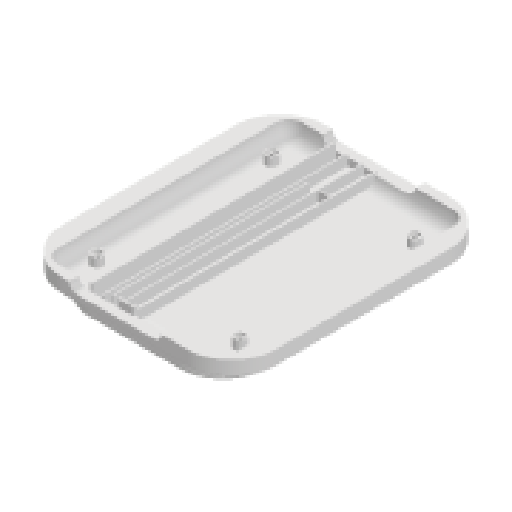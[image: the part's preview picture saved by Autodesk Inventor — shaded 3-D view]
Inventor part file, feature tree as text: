
AUTODESK INVENTOR PART (.ipt)
format: ipt  version: 2024 (Build 280153000, 153)  size: 738,304 bytes
history: native  units: mm
features: fillet x20, extrude x17, sketch x8, hole x1
ambient origin geometry x8: Origin, YZ Plane, XZ Plane, XY Plane, X Axis, Y Axis, Z Axis, Center Point
bodies: Solid1 (feature_tree)
feature tree (46):
  sketch  "Sketch1"  dims[d4=117.2mm d6=1.0mm]
  extrude  "Extrusion1"  Depth=117.2mm
  extrude  "Extrusion4"  Depth=1.0mm
  extrude  "Extrusion5"  Depth=1.0mm
  extrude  "Extrusion8"  Depth=96.0mm
  extrude  "Extrusion9"  Depth=6.8mm
  extrude  "Extrusion14"  Depth=29.9mm
  extrude  "Extrusion15"  Depth=1.0mm
  extrude  "Extrusion16"  Depth=2.0mm
  fillet  "Face Fillet21"
  fillet  "Face Fillet25"
  fillet  "Face Fillet27"
  fillet  "Face Fillet28"
  fillet  "Face Fillet29"
  fillet  "Fillet1"  Radius=177.0mm
  extrude  "Extrusion17"  Depth=2.0mm
  fillet  "Face Fillet30"
  extrude  "Extrusion19"  Depth=2.0mm
  fillet  "Fillet2"  Radius=47.0mm
  extrude  "Extrusion22"  Depth=2.0mm
  extrude  "Extrusion23"  Depth=96.0mm
  fillet  "Fillet6"  Radius=164.2mm
  fillet  "Fillet7"  Radius=12.0mm
  extrude  "Extrusion34"  Depth=2.0mm
  sketch  "Sketch10"  dims[d11=18.7mm d12=96.0mm]
  sketch  "Sketch11"  dims[d13=7.9mm d16=6.8mm]
  extrude  "Extrusion35"  Depth=2.0mm
  extrude  "Extrusion36"  Depth=10.0mm TaperAngle=0.0deg
  extrude  "Extrusion37"  Depth=2.0mm TaperAngle=0.0deg
  fillet  "Fillet8"  Radius=12.0mm
  extrude  "Extrusion38"  Depth=2.0mm TaperAngle=0.0deg
  fillet  "Face Fillet31"
  fillet  "Face Fillet32"
  fillet  "Face Fillet33"
  fillet  "Face Fillet34"
  fillet  "Fillet9"  Radius=4.0mm
  fillet  "Face Fillet35"
  fillet  "Face Fillet36"
  fillet  "Face Fillet37"
  fillet  "Face Fillet38"
  hole  "Hole1"  [1 undecoded]
  sketch  "Sketch15"  dims[d21=1.0mm d30=144.0mm d31=177.0mm d32=35.0mm d33=35.0mm d34=47.0mm d35=47.0mm d36=96.0mm d37=164.2mm d38=12.0mm d39=0.0mm d42=12.0mm d43=12.0mm d46=10.0mm d47=0.0mm d48=7.0mm d49=0.0mm d54=12.0mm d55=0.0mm d56=3.0mm d57=0.0mm d82=4.0mm d83=6.0mm d84=8.0mm d85=4.0mm d86=6.0mm d87=8.0mm d88=4.0mm d89=6.0mm d90=8.0mm d91=4.0mm d92=6.0mm d93=8.0mm d97=12.0mm d98=0.0mm d99=10.0mm d100=0.0mm d101=5.0mm d102=0.0mm d104=9.0mm d108=9.0mm d110=9.0mm d111=9.0mm d112=9.0mm d113=30.0mm d114=6.0mm d115=0.0mm d118=9.0mm d119=4.0mm d120=0.1mm d121=0.0mm d122=0.0mm d125=1.0mm d131=1.0mm d132=132.0mm d133=5.6mm d134=3.4mm d135=10.0mm d136=0.0mm d137=3.0mm d138=3.0mm d139=3.0mm d140=0.0mm d153=30.0mm d154=3.0mm d155=40.0mm d156=15.0mm d175=4.5mm d192=20.0mm d194=117.2mm d195=20.0mm d197=46.0mm d200=10.0mm d201=0.0mm d202=15.0mm d203=5.0mm d204=15.0mm d205=5.0mm d206=15.0mm d207=5.0mm d208=15.0mm d209=5.0mm d210=20.0mm d211=0.0mm d212=20.0mm d213=0.0mm d214=1.0mm d215=1.0mm d216=6.0mm d217=0.0mm d218=1.0mm d219=5.0mm d220=5.0mm d221=10.0mm d222=0.0mm d225=93.0mm d226=132.2mm d227=102.2mm d228=5.0mm d229=5.0mm d230=5.0mm d231=5.0mm d232=2.0mm d233=2.0mm d234=2.0mm d235=2.0mm d236=2.0mm d237=3.242mm d238=5.0mm d239=4.0mm d240=2.0mm d241=90.0deg d242=11.806mm d243=0.0mm d94=0.5mm d95=0.872665mm d96=0.5mm d128=20.0mm d129=0.0mm d130=0.0mm]
  sketch  "Sketch2"  dims[d7=1.0mm d8=1.0mm]
  sketch  "Sketch6"  dims[d9=1.0mm d10=1.0mm]
  sketch  "Sketch12"  dims[d17=1.0mm d18=29.9mm]
  sketch  "Sketch14"  dims[d19=3.4mm d20=1.0mm]
note: 1 required parameter value undecoded (feature->parameter linkage not recoverable at this tier; creation-order binding heuristic only, values carry confidence <= 0.55)
